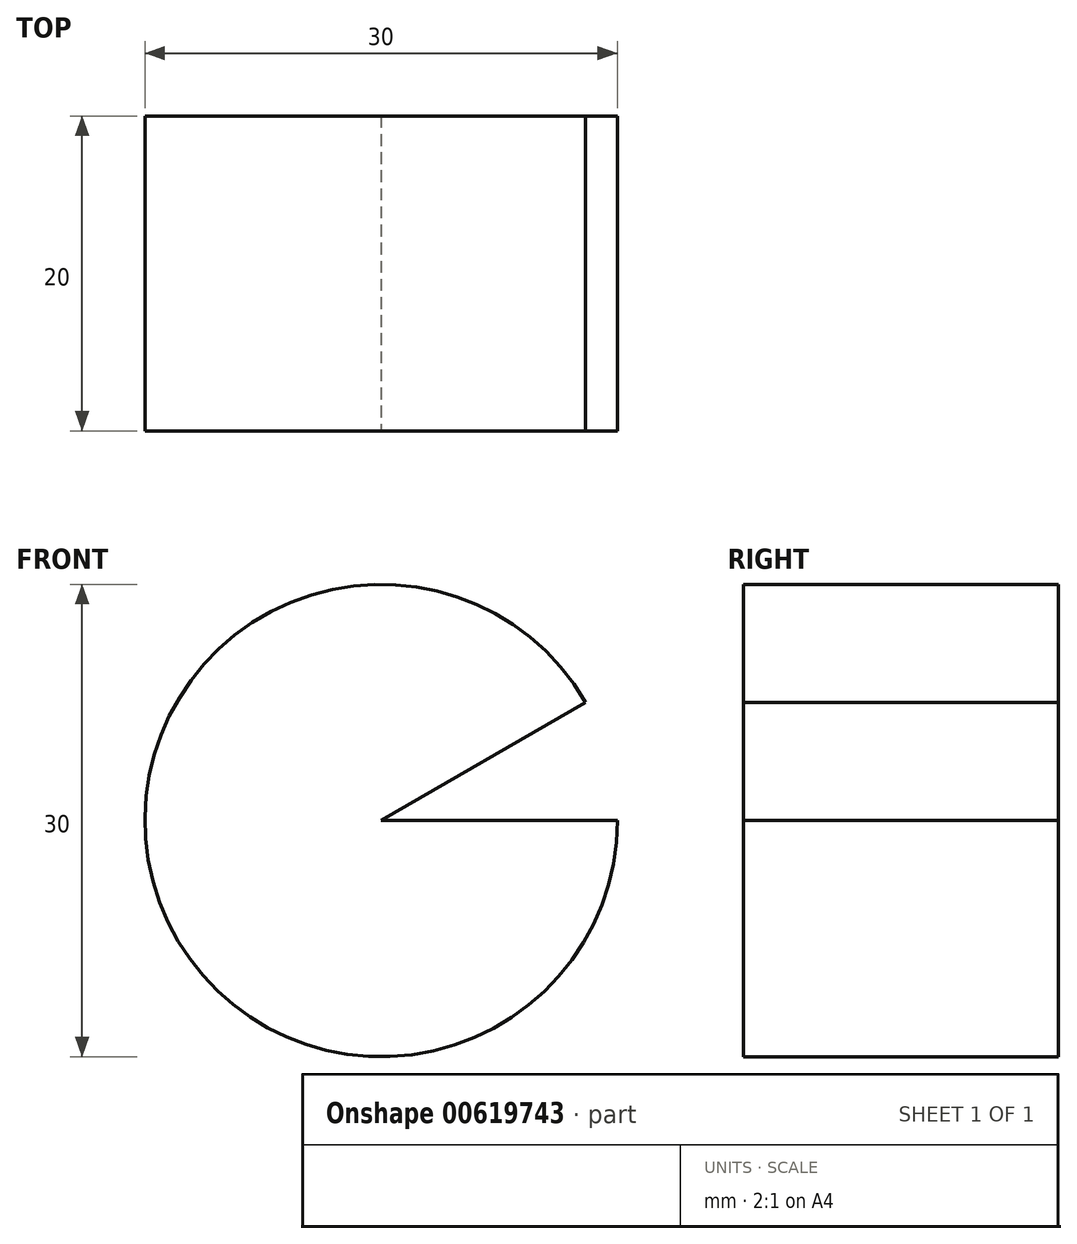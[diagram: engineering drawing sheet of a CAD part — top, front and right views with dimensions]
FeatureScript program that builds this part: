
annotation { "Feature Type Name" : "Feature", "Feature Type Description" : "" }
export const myFeature = defineFeature(function(context is Context, id is Id, definition is map)
    precondition{}
    {
        {
            var Q0;
            Q0=qCreatedBy(makeId("Top.planeOp"),FACE);
            var sketch = newSketch(context, id + "F0", { "sketchPlane" : qUnion([Q0])});
            skLineSegment(sketch, "E0.bottom", {"start": v(0, 0) * mm, "end": v(15, 0) * mm});
            skLineSegment(sketch, "E0.top", {"start": v(0, -20) * mm, "end": v(15, -20) * mm});
            skLineSegment(sketch, "E0.left", {"start": v(0, 0) * mm, "end": v(0, -20) * mm});
            skLineSegment(sketch, "E0.right", {"start": v(15, 0) * mm, "end": v(15, -20) * mm});
            skLineSegment(sketch, "E1", {"start": v(0, -10) * mm, "end": v(0, 20.7) * mm, "construction": true});
            skSolve(sketch);
        }
        {
            var Q0;
            Q0 = qSketchRegion(id + "F0", true);
            var Q1;
            Q1=sQuery(id+"F0.wireOp",EDGE,"E1");
            revolve(context, id + "F1", {"entities" : qUnion([Q0]), "axis" : qUnion([Q1]), "revolveType" : RevolveType.ONE_DIRECTION, "angle" : 330 * degree});
        }
    });
